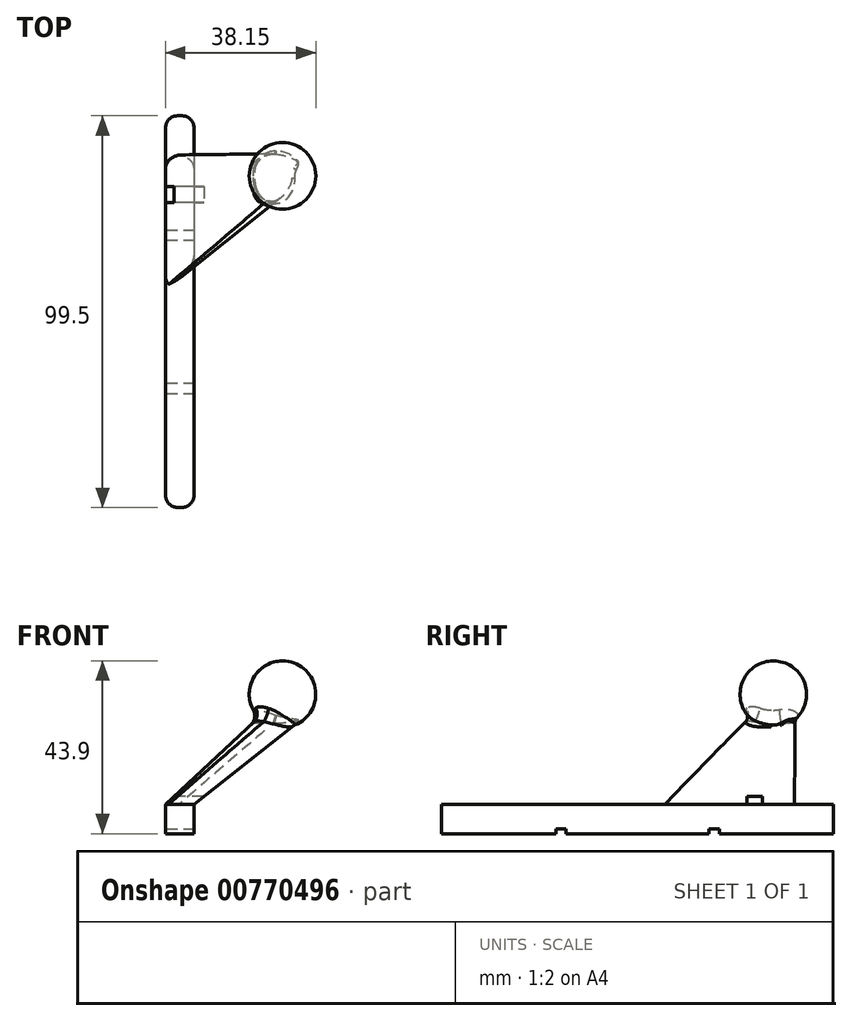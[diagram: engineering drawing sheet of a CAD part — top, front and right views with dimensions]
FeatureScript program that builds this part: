
annotation { "Feature Type Name" : "Feature", "Feature Type Description" : "" }
export const myFeature = defineFeature(function(context is Context, id is Id, definition is map)
    precondition{}
    {
        {
            var Q0;
            Q0=qCreatedBy(makeId("Top.planeOp"),FACE);
            var sketch = newSketch(context, id + "F0", { "sketchPlane" : qUnion([Q0])});
            skLineSegment(sketch, "E0.bottom", {"start": v(0.6, 49.75) * mm, "end": v(-0.6, 49.75) * mm});
            skLineSegment(sketch, "E0.top", {"start": v(0.6, -49.75) * mm, "end": v(-0.6, -49.75) * mm});
            skLineSegment(sketch, "E0.left", {"start": v(3.6, 46.75) * mm, "end": v(3.6, -46.75) * mm});
            skLineSegment(sketch, "E0.right", {"start": v(-3.6, 46.75) * mm, "end": v(-3.6, -46.75) * mm});
            skPoint(sketch, "E0.middle", {"position": v(0, 0) * mm});
            skPoint(sketch, "E1.visualSharp", {"position": v(3.6, 49.75) * mm});
            skArc(sketch, "E1.filletArc", {"start": v(3.6, 46.75) * mm, "mid": v(2.72, 48.87) * mm, "end": v(0.6, 49.75) * mm});
            skPoint(sketch, "E2.visualSharp", {"position": v(-3.6, 49.75) * mm});
            skArc(sketch, "E2.filletArc", {"start": v(-0.6, 49.75) * mm, "mid": v(-2.72, 48.87) * mm, "end": v(-3.6, 46.75) * mm});
            skPoint(sketch, "E3.visualSharp", {"position": v(3.6, -49.75) * mm});
            skArc(sketch, "E3.filletArc", {"start": v(0.6, -49.75) * mm, "mid": v(2.72, -48.87) * mm, "end": v(3.6, -46.75) * mm});
            skPoint(sketch, "E4.visualSharp", {"position": v(-3.6, -49.75) * mm});
            skArc(sketch, "E4.filletArc", {"start": v(-3.6, -46.75) * mm, "mid": v(-2.72, -48.87) * mm, "end": v(-0.6, -49.75) * mm});
            skSolve(sketch);
        }
        {
            var Q0;
            Q0=makeQuery(id+"F0.imprint","IMPRINT",FACE,{"disambiguationData":[TD([[makeQuery(id+"F0.imprint","IMPRINT",EDGE,{"derivedFrom":sQuery(id+"F0.wireOp",EDGE,"E0.bottom")}),1.0]])]});
            extrude(context, id + "F1", {"entities" : qUnion([Q0]), "depth" : 7.5 * mm, "offsetDistance" : 25 * mm});
        }
        {
            var Q0;
            Q0=makeQuery(id+"F1.opExtrude","CAP_FACE",FACE,{"disambiguationData":[OSD([sQuery(id+"F0.wireOp",EDGE,"E0.bottom"),sQuery(id+"F0.wireOp",EDGE,"E0.top"),sQuery(id+"F0.wireOp",EDGE,"E0.left"),sQuery(id+"F0.wireOp",EDGE,"E0.right"),sQuery(id+"F0.wireOp",EDGE,"E1.filletArc"),sQuery(id+"F0.wireOp",EDGE,"E2.filletArc"),sQuery(id+"F0.wireOp",EDGE,"E3.filletArc"),sQuery(id+"F0.wireOp",EDGE,"E4.filletArc")])],"isStart":true});
            var sketch = newSketch(context, id + "F2", { "sketchPlane" : qUnion([Q0])});
            skLineSegment(sketch, "E5.bottom", {"start": v(-3.6, 20.75) * mm, "end": v(3.6, 20.75) * mm});
            skLineSegment(sketch, "E5.top", {"start": v(-3.6, 18.15) * mm, "end": v(3.6, 18.15) * mm});
            skLineSegment(sketch, "E5.left", {"start": v(-3.6, 20.75) * mm, "end": v(-3.6, 18.15) * mm});
            skLineSegment(sketch, "E5.right", {"start": v(3.6, 20.75) * mm, "end": v(3.6, 18.15) * mm});
            skLineSegment(sketch, "E6.bottom", {"start": v(-3.6, -18.15) * mm, "end": v(3.6, -18.15) * mm});
            skLineSegment(sketch, "E6.top", {"start": v(-3.6, -20.75) * mm, "end": v(3.6, -20.75) * mm});
            skLineSegment(sketch, "E6.left", {"start": v(-3.6, -18.15) * mm, "end": v(-3.6, -20.75) * mm});
            skLineSegment(sketch, "E6.right", {"start": v(3.6, -18.15) * mm, "end": v(3.6, -20.75) * mm});
            skSolve(sketch);
        }
        {
            var Q0;
            Q0=qSketchRegion(id+"F2",true);
            extrude(context, id + "F3", {"entities" : qUnion([Q0]), "operationType" : NewBodyOperationType.REMOVE, "oppositeDirection" : true, "depth" : 1.2 * mm, "offsetDistance" : 25 * mm});
        }
        {
            var Q0;
            Q0=qCreatedBy(makeId("Front.planeOp"),FACE);
            var sketch = newSketch(context, id + "F4", { "sketchPlane" : qUnion([Q0])});
            skLineSegment(sketch, "E7.bottom", {"start": v(-3.6, 0) * mm, "end": v(3.6, 0) * mm, "construction": true});
            skLineSegment(sketch, "E7.top", {"start": v(-3.6, 7.5) * mm, "end": v(3.6, 7.5) * mm, "construction": true});
            skLineSegment(sketch, "E7.left", {"start": v(-3.6, 0) * mm, "end": v(-3.6, 7.5) * mm, "construction": true});
            skLineSegment(sketch, "E7.right", {"start": v(3.6, 0) * mm, "end": v(3.6, 7.5) * mm, "construction": true});
            skLineSegment(sketch, "E8", {"start": v(-3.6, 7.5) * mm, "end": v(20.53, 30) * mm});
            skLineSegment(sketch, "E9", {"start": v(20.53, 30) * mm, "end": v(32.03, 30) * mm});
            skLineSegment(sketch, "E10", {"start": v(32.03, 30) * mm, "end": v(3.6, 7.5) * mm});
            skLineSegment(sketch, "E11", {"start": v(3.6, 7.5) * mm, "end": v(-3.6, 7.5) * mm});
            skSolve(sketch);
        }
        {
            var Q0;
            Q0 = qSketchRegion(id + "F4", true);
            extrude(context, id + "F5", {"entities" : qUnion([Q0]), "oppositeDirection" : true, "depth" : 40 * mm, "offsetDistance" : 25 * mm});
        }
        {
            var Q0;
            Q0=qCreatedBy(makeId("Right.planeOp"),FACE);
            var sketch = newSketch(context, id + "F6", { "sketchPlane" : qUnion([Q0])});
            skLineSegment(sketch, "E12", {"start": v(29, 30) * mm, "end": v(6.5, 7.5) * mm});
            skLineSegment(sketch, "E13", {"start": v(6.5, 7.5) * mm, "end": v(-6.04, 7.5) * mm});
            skLineSegment(sketch, "E14", {"start": v(-6.04, 7.5) * mm, "end": v(-6.04, 30) * mm});
            skLineSegment(sketch, "E15", {"start": v(-6.04, 30) * mm, "end": v(29, 30) * mm});
            skSolve(sketch);
        }
        {
            var Q0;
            Q0 = qSketchRegion(id + "F6", true);
            extrude(context, id + "F7", {"entities" : qUnion([Q0]), "operationType" : NewBodyOperationType.REMOVE, "depth" : 75 * mm, "offsetDistance" : 25 * mm, "symmetric" : true});
        }
        {
            var Q0;
            Q0=makeQuery(id+"F7.boolean.opBoolean","INTERSECT",EDGE,{"derivedFrom":[makeQuery(id+"F5.opExtrude","SWEPT_FACE",FACE,{"disambiguationData":[OSD([sQuery(id+"F4.wireOp",EDGE,"E8")])]}),makeQuery(id+"F7.opExtrude","SWEPT_FACE",FACE,{"disambiguationData":[OSD([sQuery(id+"F6.wireOp",EDGE,"E12")])]})]});
            var Q1;
            Q1=makeQuery(id+"F7.boolean.opBoolean","INTERSECT",EDGE,{"derivedFrom":[makeQuery(id+"F5.opExtrude","SWEPT_FACE",FACE,{"disambiguationData":[OSD([sQuery(id+"F4.wireOp",EDGE,"E10")])]}),makeQuery(id+"F7.opExtrude","SWEPT_FACE",FACE,{"disambiguationData":[OSD([sQuery(id+"F6.wireOp",EDGE,"E12")])]})]});
            var Q2;
            Q2=makeQuery(id+"F5.opExtrude","CAP_EDGE",EDGE,{"disambiguationData":[OSD([sQuery(id+"F4.wireOp",EDGE,"E10")])],"isStart":false});
            var Q3;
            Q3=makeQuery(id+"F5.opExtrude","CAP_EDGE",EDGE,{"disambiguationData":[OSD([sQuery(id+"F4.wireOp",EDGE,"E8")])],"isStart":false});
            fillet(context, id + "F8", {"entities" : qUnion([Q0, Q1, Q2, Q3]), "radius" : 3.5 * mm, "tangentPropagation" : true, "allowEdgeOverflow" : false});
        }
        {
            var Q0;
            Q0=qCreatedBy(makeId("Front.planeOp"),FACE);
            cPlane(context, id + "F9", {"entities" : qUnion([Q0]), "cplaneType" : CPlaneType.OFFSET, "offset" : 34.5 * mm, "oppositeDirection" : true, "width" : 150 * mm, "height" : 150 * mm});
        }
        {
            var Q0;
            Q0=qCreatedBy(id+"F9.planeOp",FACE);
            var sketch = newSketch(context, id + "F10", { "sketchPlane" : qUnion([Q0])});
            skLineSegment(sketch, "E16", {"start": v(26.1, 27) * mm, "end": v(26.1, 43.9) * mm});
            skArc(sketch, "E17", {"start": v(26.1, 43.9) * mm, "mid": v(17.65, 35.45) * mm, "end": v(26.1, 27) * mm});
            skSolve(sketch);
        }
        {
            var Q0;
            Q0 = qSketchRegion(id + "F10", true);
            var Q1;
            Q1=sQuery(id+"F10.wireOp",EDGE,"E16");
            revolve(context, id + "F11", {"operationType" : NewBodyOperationType.ADD, "surfaceOperationType" : NewSurfaceOperationType.NEW, "entities" : qUnion([Q0]), "axis" : qUnion([Q1]), "revolveType" : RevolveType.FULL});
        }
        {
            var Q0;
            Q0=makeQuery(id+"F1.opExtrude","SWEPT_FACE",FACE,{"disambiguationData":[OSD([sQuery(id+"F0.wireOp",EDGE,"E0.right")])]});
            var sketch = newSketch(context, id + "F12", { "sketchPlane" : qUnion([Q0])});
            skLineSegment(sketch, "E18.bottom", {"start": v(-31.75, 7.5) * mm, "end": v(-27.75, 7.5) * mm});
            skLineSegment(sketch, "E18.top", {"start": v(-31.75, 9.5) * mm, "end": v(-27.75, 9.5) * mm});
            skLineSegment(sketch, "E18.left", {"start": v(-31.75, 7.5) * mm, "end": v(-31.75, 9.5) * mm});
            skLineSegment(sketch, "E18.right", {"start": v(-27.75, 7.5) * mm, "end": v(-27.75, 9.5) * mm});
            skSolve(sketch);
        }
        {
            var Q0;
            Q0 = qSketchRegion(id + "F12", true);
            extrude(context, id + "F13", {"entities" : qUnion([Q0]), "operationType" : NewBodyOperationType.REMOVE, "oppositeDirection" : true, "depth" : 25 * mm, "offsetDistance" : 25 * mm});
        }
        {
            var Q0;
            Q0=makeQuery(id+"F11.boolean.opBoolean","INTERSECT",EDGE,{"derivedFrom":[makeQuery(id+"F8.opFillet","BLEND_FACE",FACE,{"disambiguationData":[OSD([sQuery(id+"F4.wireOp",EDGE,"E10")])]}),makeQuery(id+"F11.opRevolve","SWEPT_FACE",FACE,{"disambiguationData":[OSD([sQuery(id+"F10.wireOp",EDGE,"E17")])]})]});
            var Q1;
            Q1=makeQuery(id+"F11.boolean.opBoolean","INTERSECT",EDGE,{"derivedFrom":[makeQuery(id+"F8.opFillet","BLEND_FACE",FACE,{"disambiguationData":[OSD([sQuery(id+"F4.wireOp",EDGE,"E8")])]}),makeQuery(id+"F11.opRevolve","SWEPT_FACE",FACE,{"disambiguationData":[OSD([sQuery(id+"F10.wireOp",EDGE,"E17")])]})]});
            fillet(context, id + "F14", {"entities" : qUnion([Q0, Q1]), "radius" : 3 * mm, "tangentPropagation" : true, "allowEdgeOverflow" : false});
        }
    });
